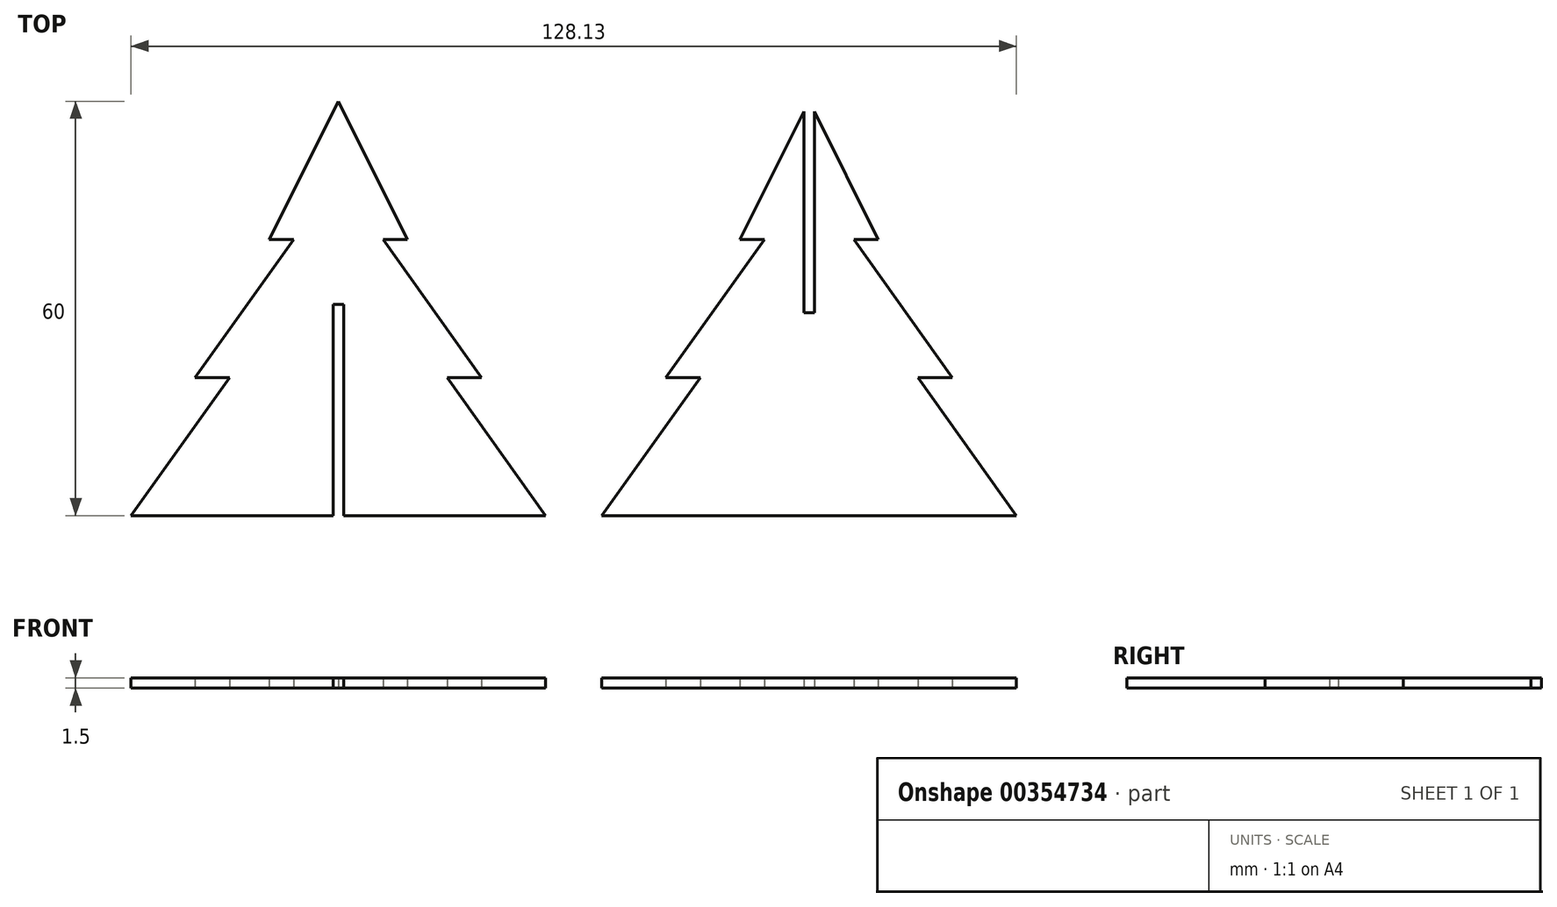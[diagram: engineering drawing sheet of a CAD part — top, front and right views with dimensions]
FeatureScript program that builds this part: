
annotation { "Feature Type Name" : "Feature", "Feature Type Description" : "" }
export const myFeature = defineFeature(function(context is Context, id is Id, definition is map)
    precondition{}
    {
        {
            var Q0;
            Q0=qCreatedBy(makeId("Top.planeOp"),FACE);
            var sketch = newSketch(context, id + "F0", { "sketchPlane" : qUnion([Q0])});
            skLineSegment(sketch, "E0", {"start": v(30, 0) * mm, "end": v(15.74, 20) * mm});
            skLineSegment(sketch, "E1", {"start": v(15.74, 20) * mm, "end": v(20.74, 20) * mm});
            skLineSegment(sketch, "E2", {"start": v(20.74, 20) * mm, "end": v(6.47, 40) * mm});
            skLineSegment(sketch, "E3", {"start": v(6.47, 40) * mm, "end": v(10, 40) * mm});
            skLineSegment(sketch, "E4.MirrorCS", {"start": v(-6.47, 40) * mm, "end": v(-10, 40) * mm});
            skLineSegment(sketch, "E5.MirrorCS", {"start": v(-20.74, 20) * mm, "end": v(-6.47, 40) * mm});
            skLineSegment(sketch, "E6.MirrorCS", {"start": v(-15.74, 20) * mm, "end": v(-20.74, 20) * mm});
            skLineSegment(sketch, "E7.MirrorCS", {"start": v(-30, 0) * mm, "end": v(-15.74, 20) * mm});
            skLineSegment(sketch, "E8", {"start": v(-34.06, 66.03) * mm, "end": v(-34.06, 0) * mm, "construction": true});
            skLineSegment(sketch, "E9.MirrorCS", {"start": v(-58.13, 40) * mm, "end": v(-68.13, 60) * mm});
            skLineSegment(sketch, "E10.MirrorCS", {"start": v(-78.13, 40) * mm, "end": v(-68.13, 60) * mm});
            skLineSegment(sketch, "E11.MirrorCS", {"start": v(-74.6, 40) * mm, "end": v(-78.13, 40) * mm});
            skLineSegment(sketch, "E12.MirrorCS", {"start": v(-61.66, 40) * mm, "end": v(-58.13, 40) * mm});
            skLineSegment(sketch, "E13.MirrorCS", {"start": v(-47.4, 20) * mm, "end": v(-61.66, 40) * mm});
            skLineSegment(sketch, "E14.MirrorCS", {"start": v(-88.87, 20) * mm, "end": v(-74.6, 40) * mm});
            skLineSegment(sketch, "E15.MirrorCS", {"start": v(-52.4, 20) * mm, "end": v(-47.4, 20) * mm});
            skLineSegment(sketch, "E16.MirrorCS", {"start": v(-83.87, 20) * mm, "end": v(-88.87, 20) * mm});
            skLineSegment(sketch, "E17.MirrorCS", {"start": v(-98.13, 0) * mm, "end": v(-83.87, 20) * mm});
            skLineSegment(sketch, "E18.MirrorCS", {"start": v(-38.13, 0) * mm, "end": v(-52.4, 20) * mm});
            skLineSegment(sketch, "E19", {"start": v(-10, 40) * mm, "end": v(-0.75, 58.5) * mm});
            skLineSegment(sketch, "E20", {"start": v(0.75, 58.5) * mm, "end": v(10, 40) * mm});
            skLineSegment(sketch, "E21", {"start": v(-98.13, 0) * mm, "end": v(-68.88, 0) * mm});
            skLineSegment(sketch, "E22", {"start": v(-67.38, 0) * mm, "end": v(-38.13, 0) * mm});
            skLineSegment(sketch, "E23", {"start": v(-30, 0) * mm, "end": v(30, 0) * mm});
            skLineSegment(sketch, "E24", {"start": v(-68.88, 30.59) * mm, "end": v(-67.38, 30.59) * mm});
            skLineSegment(sketch, "E25", {"start": v(-0.75, 29.34) * mm, "end": v(0.75, 29.34) * mm});
            skLineSegment(sketch, "E26", {"start": v(-0.75, 58.5) * mm, "end": v(-0.75, 29.34) * mm});
            skLineSegment(sketch, "E27", {"start": v(0.75, 58.5) * mm, "end": v(0.75, 29.34) * mm});
            skLineSegment(sketch, "E28", {"start": v(-68.88, 30.59) * mm, "end": v(-68.88, 0) * mm});
            skLineSegment(sketch, "E29", {"start": v(-67.38, 30.59) * mm, "end": v(-67.38, 0) * mm});
            skSolve(sketch);
        }
        {
            var Q0;
            Q0 = qSketchRegion(id + "F0", true);
            extrude(context, id + "F1", {"entities" : qUnion([Q0]), "depth" : 1.5 * mm});
        }
    });
